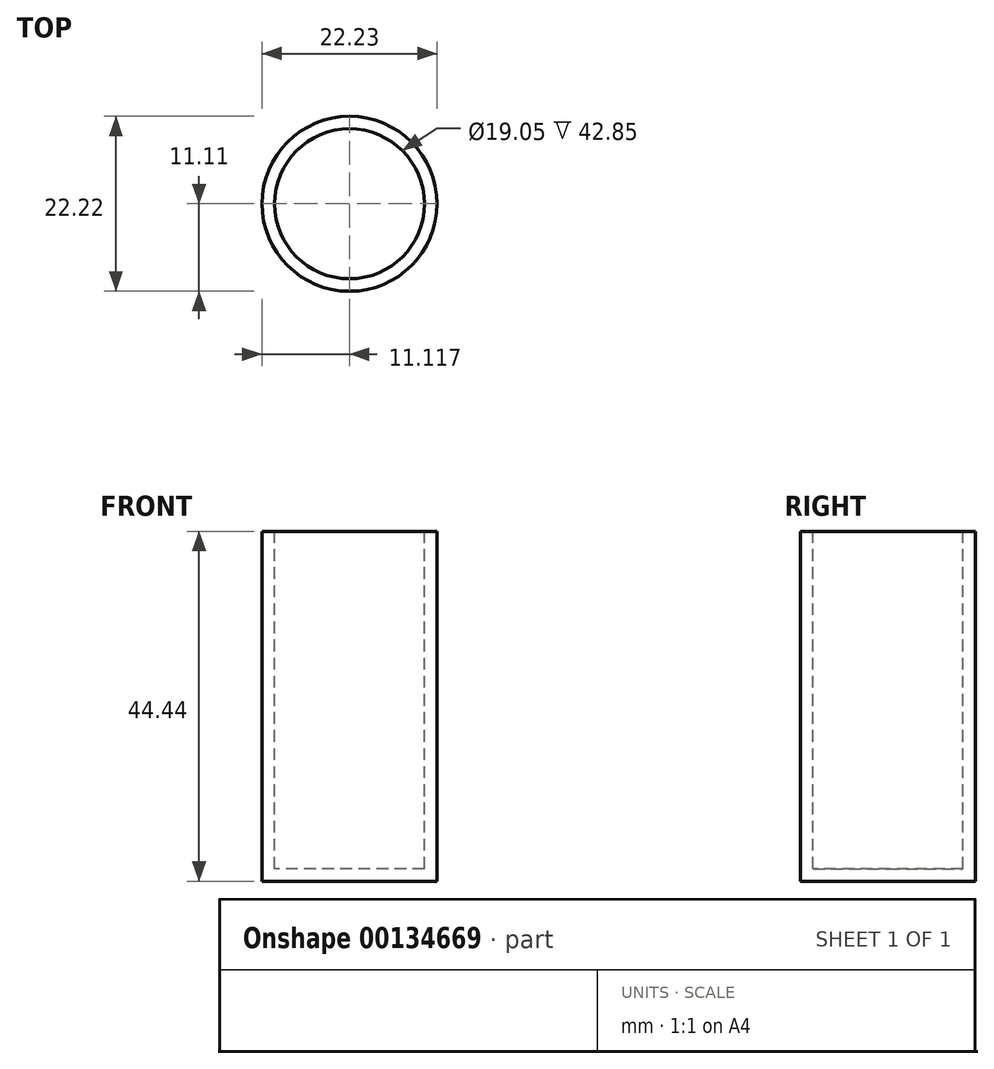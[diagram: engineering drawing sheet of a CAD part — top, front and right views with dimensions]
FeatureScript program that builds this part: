
annotation { "Feature Type Name" : "Feature", "Feature Type Description" : "" }
export const myFeature = defineFeature(function(context is Context, id is Id, definition is map)
    precondition{}
    {
        {
            var Q0;
            Q0=qCreatedBy(makeId("Front.planeOp"),FACE);
            var sketch = newSketch(context, id + "F0", { "sketchPlane" : qUnion([Q0])});
            skLineSegment(sketch, "E0", {"start": v(-5.05, 0) * mm, "end": v(-16.17, 0) * mm});
            skLineSegment(sketch, "E1", {"start": v(-16.17, 0) * mm, "end": v(-16.17, 44.44) * mm});
            skLineSegment(sketch, "E2", {"start": v(-16.17, 44.44) * mm, "end": v(-14.58, 44.44) * mm});
            skLineSegment(sketch, "E3", {"start": v(-14.58, 44.44) * mm, "end": v(-14.58, 1.59) * mm});
            skLineSegment(sketch, "E4", {"start": v(-14.58, 1.59) * mm, "end": v(-5.05, 1.59) * mm});
            skLineSegment(sketch, "E5", {"start": v(-5.05, 1.59) * mm, "end": v(-5.05, 0) * mm});
            skSolve(sketch);
        }
        {
            var Q0;
            Q0 = qSketchRegion(id + "F0", true);
            var Q1;
            Q1=sQuery(id+"F0.wireOp",EDGE,"E5");
            revolve(context, id + "F1", {"entities" : qUnion([Q0]), "axis" : qUnion([Q1]), "revolveType" : RevolveType.FULL});
        }
    });
